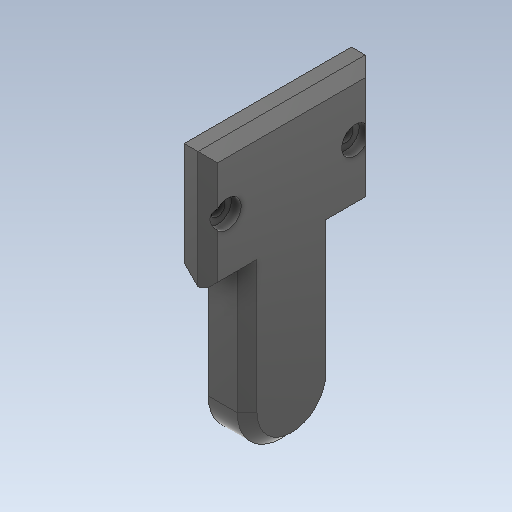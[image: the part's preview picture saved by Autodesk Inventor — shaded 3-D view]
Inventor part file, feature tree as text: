
AUTODESK INVENTOR PART (.ipt)
format: ipt  version: 2020 (Build 240168000, 168)  size: 505,856 bytes
history: native  units: mm
features: extrude x20, sketch x18, reference x8, projected_geometry x7, other x6, chamfer x5, plane x2, hole x1, mirror x1, delete_face x1
ambient origin geometry x8: Origin, YZ Plane, XZ Plane, XY Plane, X Axis, Y Axis, Z Axis, Center Point
bodies: Solid1 (feature_tree), Solid2 (feature_tree)
feature tree (69):
  extrude  "Extrusion1"  Depth=18.0mm
  plane  "Work Plane1"
  extrude  "Extrusion2"  Depth=18.0mm
  extrude  "Extrusion3"  Depth=2.0mm TaperAngle=0.0deg
  extrude  "Extrusion4"  TaperAngle=0.0deg  [1 undecoded]
  extrude  "Extrusion5"  Depth=50.1mm TaperAngle=0.0deg
  sketch  "Sketch6"  dims[d14=7.199887mm d15=3.599976mm]
  extrude  "Extrusion6"  Depth=3.599976mm
  extrude  "Extrusion7"  Depth=0.15mm
  extrude  "Extrusion8"  Depth=0.15mm
  extrude  "Extrusion10"  Depth=15.9mm TaperAngle=0.0deg
  extrude  "Extrusion11"  Depth=6.5mm
  extrude  "Extrusion12"  Depth=3.925mm
  extrude  "Extrusion13"  Depth=5.15mm
  sketch  "Sketch14"  dims[d29=2.525mm d30=5.15mm]
  extrude  "Extrusion14"  Depth=12.55mm
  extrude  "Extrusion15"  Depth=2.75mm TaperAngle=0.0deg
  hole  "Hole1"  [1 undecoded]
  extrude  "Extrusion16"  Depth=2.525mm
  plane  "Work Plane2"
  mirror  "Mirror1"
  delete_face  "Delete Face2"
  extrude  "Extrusion18"  Depth=23.15mm
  extrude  "Extrusion19"  Depth=10.0mm
  extrude  "Extrusion20"  TaperAngle=0.0deg  [1 undecoded]
  extrude  "Extrusion21"  Depth=2.0mm
  chamfer  "Chamfer1"  Distance=19.0mm
  chamfer  "Chamfer2"  [1 undecoded]
  chamfer  "Chamfer3"  Distance=8.8mm
  extrude  "Extrusion22"  Depth=2.0mm
  chamfer  "Chamfer4"  Distance=2.525mm
  chamfer  "Chamfer5"  Distance=23.15mm
  sketch  "Sketch1"  dims[d0=18.0mm d1=45.0mm]
  reference  "Reference1"
  sketch  "Sketch2"  dims[d2=45.0mm d3=18.0mm]
  reference  "Reference2"
  sketch  "Sketch3"  dims[d4=18.0mm d5=51.1mm d6=2.0mm d7=0.0mm d8=0.0mm]
  reference  "Reference3"
  reference  "Reference4"
  reference  "Reference5"
  reference  "Reference6"
  reference  "Reference7"
  reference  "Reference8"
  sketch  "Sketch4"  dims[d9=37.3mm d10=0.0mm]
  sketch  "Sketch5"  dims[d11=35.0mm d12=50.1mm d13=0.0mm]
  sketch  "Sketch8"  dims[d16=0.15mm d17=0.15mm]
  sketch  "Sketch10"  dims[d18=0.15mm d19=0.15mm]
  sketch  "Sketch11"  dims[d20=5.4mm d21=0.0mm d22=15.9mm d23=0.0mm]
  sketch  "Sketch12"  dims[d24=6.5mm d25=0.0mm d26=23.15mm]
  sketch  "Sketch13"  dims[d27=12.55mm d28=3.925mm]
  sketch  "Sketch15"  dims[d31=5.15mm d32=12.55mm]
  sketch  "Sketch17"  dims[d33=40.75mm d34=0.0mm d35=2.75mm d36=0.0mm]
  other  "Pattern of Solid1:1"
  sketch  "Sketch19"  dims[d43=11.85mm d44=23.15mm]
  projected_geometry  "Projected Loop1"
  sketch  "Sketch20"  dims[d45=3.925mm d46=2.525mm]
  projected_geometry  "Projected Loop2"
  sketch  "Sketch21"  dims[d47=12.55mm d48=23.15mm]
  projected_geometry  "Projected Loop3"
  projected_geometry  "Projected Loop4"
  projected_geometry  "Projected Loop5"
  projected_geometry  "Projected Loop6"
  sketch  "Sketch23"  dims[d49=10.05mm d50=0.0mm d54=10.0mm d55=0.0mm d56=0.0mm d57=19.0mm d58=0.0mm d59=8.8mm d60=5.925mm d61=2.525mm d62=23.15mm d63=15.075mm d64=23.15mm d65=6.05mm d66=23.15mm d67=12.55mm d68=0.0mm d72=8.8mm d73=10.0mm d74=10.2mm d75=17.225mm d76=4.0mm d77=0.0mm d78=3.85mm d79=10.925mm d80=5.0mm d81=0.0mm d82=0.765mm d83=1.0mm d84=0.0mm d85=18.0mm d86=5.0mm d87=5.0mm d88=53.1mm d89=0.0mm d90=53.1mm d91=0.0mm d92=3.0mm d93=6.0mm d94=4.0mm d95=2.0mm d96=90.0deg d97=40.0mm d98=0.0mm d99=3.1mm d100=2.4mm d101=0.0mm d105=3.1mm d106=2.4mm d107=0.0mm d108=8.0mm d109=8.0mm d110=24.0mm d111=3.0mm d112=3.0mm d113=26.0mm d114=4.0mm d115=4.0mm d116=12.0mm d117=10.0mm d118=0.0mm d119=3.1mm d120=3.1mm d121=2.4mm d122=0.0mm d123=51.141786mm d124=30.859708mm d125=100.0mm d126=0.0mm d127=3.0mm d128=2.0mm d129=45.0deg d130=0.01mm d131=2.0mm d132=45.0deg d133=3.0mm d134=2.0mm d135=45.0deg d136=5.6mm d137=5.6mm d138=2.0mm d139=0.0mm d140=2.0mm d141=2.0mm d142=45.0deg d143=1.0mm d144=2.0mm d145=45.0deg]
  projected_geometry  "Projected Loop7"
  parser-record x1  (decoder bookkeeping rows leaked as tree rows — omitted from the tree; the rows remain in map.json)
  other  "Demo2.0004.iam"
  other  "Bearing:2"
  other  "Rolling bearing GB/T 7218-1995 Type FSN 70000-Z F 623-Z:1"
  other  "servo horn 1:1"
note: 4 required parameter values undecoded (feature->parameter linkage not recoverable at this tier; creation-order binding heuristic only, values carry confidence <= 0.55)
note: 1 file-system path scrubbed to <path> (originals preserved in map.json)
